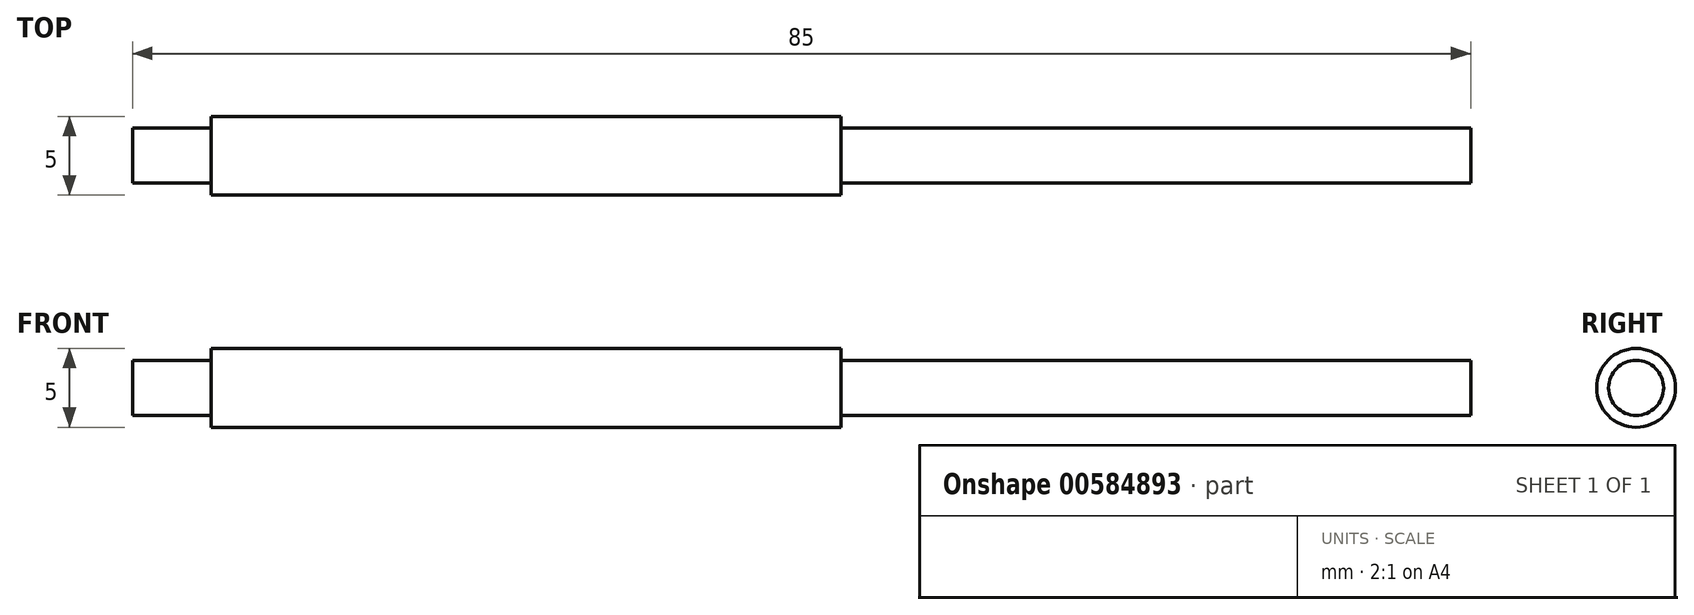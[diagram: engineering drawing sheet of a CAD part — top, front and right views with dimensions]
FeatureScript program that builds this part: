
annotation { "Feature Type Name" : "Feature", "Feature Type Description" : "" }
export const myFeature = defineFeature(function(context is Context, id is Id, definition is map)
    precondition{}
    {
        {
            var Q0;
            Q0=qCreatedBy(makeId("Top.planeOp"),FACE);
            var sketch = newSketch(context, id + "F0", { "sketchPlane" : qUnion([Q0])});
            skLineSegment(sketch, "E0.bottom", {"start": v(-20, 15) * mm, "end": v(20, 15) * mm});
            skLineSegment(sketch, "E0.top", {"start": v(-20, 0) * mm, "end": v(20, 0) * mm});
            skLineSegment(sketch, "E0.left", {"start": v(-20, 15) * mm, "end": v(-20, 0) * mm});
            skLineSegment(sketch, "E0.right", {"start": v(20, 15) * mm, "end": v(20, 0) * mm});
            skPoint(sketch, "E0.middle", {"position": v(0, 7.5) * mm});
            skSolve(sketch);
        }
        {
            var Q0;
            Q0 = qSketchRegion(id + "F0", true);
            var Q1;
            Q1=sQuery(id+"F0.wireOp",EDGE,"E0.top");
            revolve(context, id + "F1", {"entities" : qUnion([Q0]), "axis" : qUnion([Q1]), "revolveType" : RevolveType.FULL});
        }
        {
            var Q0;
            Q0=makeQuery(id+"F1.opRevolve","SWEPT_FACE",FACE,{"disambiguationData":[OSD([sQuery(id+"F0.wireOp",EDGE,"E0.right")])]});
            var sketch = newSketch(context, id + "F2", { "sketchPlane" : qUnion([Q0])});
            skCircle(sketch, "E1", {"center": v(0, 0) * mm, "radius": 1.75 * mm});
            skCircle(sketch, "E2.0", {"center": v(0, 0) * mm, "radius": 15 * mm});
            skLineSegment(sketch, "E3", {"start": v(-10.07, -11.12) * mm, "end": v(-0.6, -1.65) * mm});
            skLineSegment(sketch, "E4", {"start": v(-11.13, -10.06) * mm, "end": v(-1.65, -0.58) * mm});
            skLineSegment(sketch, "E5", {"start": v(-14.98, 0.75) * mm, "end": v(-1.58, 0.75) * mm});
            skLineSegment(sketch, "E6", {"start": v(-14.98, -0.75) * mm, "end": v(-1.58, -0.75) * mm});
            skLineSegment(sketch, "E7", {"start": v(-0.75, 14.98) * mm, "end": v(-0.75, 1.58) * mm});
            skLineSegment(sketch, "E8", {"start": v(0.75, -14.98) * mm, "end": v(0.75, -1.58) * mm});
            skLineSegment(sketch, "E9.MirrorCS", {"start": v(-0.75, -14.98) * mm, "end": v(-0.75, -1.58) * mm});
            skLineSegment(sketch, "E10.MirrorCS", {"start": v(11.13, -10.06) * mm, "end": v(1.65, -0.58) * mm});
            skLineSegment(sketch, "E11.MirrorCS", {"start": v(10.07, -11.12) * mm, "end": v(0.6, -1.65) * mm});
            skCircle(sketch, "E12", {"center": v(0, 0) * mm, "radius": 2.5 * mm});
            skLineSegment(sketch, "E13.trimOffspring", {"start": v(-1.65, 0.6) * mm, "end": v(-11.12, 10.07) * mm});
            skLineSegment(sketch, "E14.trimOffspring", {"start": v(0.58, 1.65) * mm, "end": v(10.06, 11.13) * mm});
            skLineSegment(sketch, "E15.trimOffspring", {"start": v(1.58, 0.75) * mm, "end": v(14.98, 0.75) * mm});
            skLineSegment(sketch, "E16.trimOffspring", {"start": v(-0.75, 1.58) * mm, "end": v(-0.75, 14.98) * mm});
            skLineSegment(sketch, "E17.trimOffspring", {"start": v(-0.75, -1.58) * mm, "end": v(-0.75, -14.98) * mm});
            skLineSegment(sketch, "E18.trimOffspring", {"start": v(-0.58, 1.65) * mm, "end": v(-10.06, 11.13) * mm});
            skLineSegment(sketch, "E19.trimOffspring", {"start": v(0.75, 1.58) * mm, "end": v(0.75, 14.98) * mm});
            skLineSegment(sketch, "E20.trimOffspring", {"start": v(1.65, 0.6) * mm, "end": v(11.12, 10.07) * mm});
            skLineSegment(sketch, "E21.trimOffspring", {"start": v(1.58, -0.75) * mm, "end": v(14.98, -0.75) * mm});
            skSolve(sketch);
        }
        {
            var Q0;
            {var subQ0=sQuery(id+"F2.wireOp",EDGE,"E1");var subQ8=makeQuery(id+"F2.imprint","INTERSECT",VERTEX,{"derivedFrom":[subQ0,sQuery(id+"F2.wireOp",EDGE,"E15.trimOffspring")]});Q0=makeQuery(id+"F2.imprint","IMPRINT",FACE,{"disambiguationData":[TD([[makeQuery(id+"F2.imprint","IMPRINT",EDGE,{"disambiguationData":[TD([[subQ8,1.0]])],"derivedFrom":subQ0}),1.0]])]});}
            var Q1;
            {var subQ0=sQuery(id+"F2.wireOp",EDGE,"E15.trimOffspring");var subQ1=sQuery(id+"F2.wireOp",EDGE,"E2.0");var subQ2=makeQuery(id+"F2.imprint","INTERSECT",VERTEX,{"derivedFrom":[subQ1,subQ0]});Q1=makeQuery(id+"F2.imprint","IMPRINT",FACE,{"disambiguationData":[TD([[makeQuery(id+"F2.imprint","IMPRINT",EDGE,{"disambiguationData":[TD([[subQ2,1.0]])],"derivedFrom":subQ1}),-1.0]])]});}
            var Q2;
            {var subQ0=sQuery(id+"F2.wireOp",EDGE,"E10.MirrorCS");var subQ1=sQuery(id+"F2.wireOp",EDGE,"E2.0");var subQ2=makeQuery(id+"F2.imprint","INTERSECT",VERTEX,{"derivedFrom":[subQ1,subQ0]});Q2=makeQuery(id+"F2.imprint","IMPRINT",FACE,{"disambiguationData":[TD([[makeQuery(id+"F2.imprint","IMPRINT",EDGE,{"disambiguationData":[TD([[subQ2,1.0]])],"derivedFrom":subQ1}),-1.0]])]});}
            var Q3;
            {var subQ0=sQuery(id+"F2.wireOp",EDGE,"E8");var subQ1=sQuery(id+"F2.wireOp",EDGE,"E2.0");var subQ2=makeQuery(id+"F2.imprint","INTERSECT",VERTEX,{"derivedFrom":[subQ1,subQ0]});Q3=makeQuery(id+"F2.imprint","IMPRINT",FACE,{"disambiguationData":[TD([[makeQuery(id+"F2.imprint","IMPRINT",EDGE,{"disambiguationData":[TD([[subQ2,1.0]])],"derivedFrom":subQ1}),-1.0]])]});}
            var Q4;
            {var subQ0=sQuery(id+"F2.wireOp",EDGE,"E3");var subQ1=sQuery(id+"F2.wireOp",EDGE,"E2.0");var subQ2=makeQuery(id+"F2.imprint","INTERSECT",VERTEX,{"derivedFrom":[subQ1,subQ0]});Q4=makeQuery(id+"F2.imprint","IMPRINT",FACE,{"disambiguationData":[TD([[makeQuery(id+"F2.imprint","IMPRINT",EDGE,{"disambiguationData":[TD([[subQ2,1.0]])],"derivedFrom":subQ1}),-1.0]])]});}
            var Q5;
            {var subQ0=sQuery(id+"F2.wireOp",EDGE,"E4");var subQ1=sQuery(id+"F2.wireOp",EDGE,"E2.0");var subQ2=makeQuery(id+"F2.imprint","INTERSECT",VERTEX,{"derivedFrom":[subQ1,subQ0]});Q5=makeQuery(id+"F2.imprint","IMPRINT",FACE,{"disambiguationData":[TD([[makeQuery(id+"F2.imprint","IMPRINT",EDGE,{"disambiguationData":[TD([[subQ2,-1.0]])],"derivedFrom":subQ1}),-1.0]])]});}
            var Q6;
            {var subQ0=sQuery(id+"F2.wireOp",EDGE,"E5");var subQ1=sQuery(id+"F2.wireOp",EDGE,"E2.0");var subQ2=makeQuery(id+"F2.imprint","INTERSECT",VERTEX,{"derivedFrom":[subQ1,subQ0]});Q6=makeQuery(id+"F2.imprint","IMPRINT",FACE,{"disambiguationData":[TD([[makeQuery(id+"F2.imprint","IMPRINT",EDGE,{"disambiguationData":[TD([[subQ2,-1.0]])],"derivedFrom":subQ1}),-1.0]])]});}
            var Q7;
            {var subQ0=sQuery(id+"F2.wireOp",EDGE,"E16.trimOffspring");var subQ1=sQuery(id+"F2.wireOp",EDGE,"E2.0");var subQ2=makeQuery(id+"F2.imprint","INTERSECT",VERTEX,{"derivedFrom":[subQ1,subQ0]});Q7=makeQuery(id+"F2.imprint","IMPRINT",FACE,{"disambiguationData":[TD([[makeQuery(id+"F2.imprint","IMPRINT",EDGE,{"disambiguationData":[TD([[subQ2,1.0]])],"derivedFrom":subQ1}),-1.0]])]});}
            var Q8;
            {var subQ0=sQuery(id+"F2.wireOp",EDGE,"E14.trimOffspring");var subQ1=sQuery(id+"F2.wireOp",EDGE,"E2.0");var subQ2=makeQuery(id+"F2.imprint","INTERSECT",VERTEX,{"derivedFrom":[subQ1,subQ0]});Q8=makeQuery(id+"F2.imprint","IMPRINT",FACE,{"disambiguationData":[TD([[makeQuery(id+"F2.imprint","IMPRINT",EDGE,{"disambiguationData":[TD([[subQ2,1.0]])],"derivedFrom":subQ1}),-1.0]])]});}
            extrude(context, id + "F3", {"entities" : qUnion([Q0, Q1, Q2, Q3, Q4, Q5, Q6, Q7, Q8]), "operationType" : NewBodyOperationType.REMOVE, "endBound" : BoundingType.THROUGH_ALL, "oppositeDirection" : true, "depth" : 25 * mm, "offsetDistance" : 25 * mm});
        }
        {
            var Q0;
            Q0=makeQuery(id+"F1.opRevolve","SWEPT_FACE",FACE,{"disambiguationData":[OSD([sQuery(id+"F0.wireOp",EDGE,"E0.left")])]});
            var sketch = newSketch(context, id + "F4", { "sketchPlane" : qUnion([Q0])});
            skCircle(sketch, "E22", {"center": v(0, 0) * mm, "radius": 0.75 * mm});
            skSolve(sketch);
        }
        {
            var Q0;
            {var subQ2=sQuery(id+"F0.wireOp",EDGE,"E0.left");var subQ3=makeQuery(id+"F1.opRevolve","SWEPT_FACE",FACE,{"disambiguationData":[OSD([subQ2])]});Q0=makeQuery(id+"F4.imprint","IMPRINT",FACE,{"disambiguationData":[TD([[makeQuery(id+"F4.imprint","IMPRINT",EDGE,{"derivedFrom":makeQuery(id+"F3.boolean.opBoolean","INTERSECT",EDGE,{"derivedFrom":[subQ3,makeQuery(id+"F3.opExtrude","SWEPT_FACE",FACE,{"disambiguationData":[OSD([sQuery(id+"F2.wireOp",EDGE,"E1")])]})]})}),1.0]])]});}
            var sketch = newSketch(context, id + "F5", { "sketchPlane" : qUnion([Q0])});
            skCircle(sketch, "E23.0", {"center": v(0, 0) * mm, "radius": 1.75 * mm});
            skCircle(sketch, "E24.cCircle", {"center": v(0, 0) * mm, "radius": 1.75 * mm, "construction": true});
            skLineSegment(sketch, "E24.0", {"start": v(0.78, -1.57) * mm, "end": v(-1.75, 0.11) * mm});
            skLineSegment(sketch, "E24.1", {"start": v(-1.75, 0.11) * mm, "end": v(0.97, 1.46) * mm});
            skLineSegment(sketch, "E24.2", {"start": v(0.97, 1.46) * mm, "end": v(0.78, -1.57) * mm});
            skSolve(sketch);
        }
        {
            var Q0;
            Q0=makeQuery(id+"F4.imprint","IMPRINT",FACE,{"disambiguationData":[TD([[makeQuery(id+"F4.imprint","IMPRINT",EDGE,{"derivedFrom":sQuery(id+"F4.wireOp",EDGE,"E22")}),-1.0]])]});
            var Q1;
            Q1=makeQuery(id+"F4.imprint","IMPRINT",FACE,{"disambiguationData":[TD([[makeQuery(id+"F4.imprint","IMPRINT",EDGE,{"derivedFrom":sQuery(id+"F4.wireOp",EDGE,"E22")}),1.0]])]});
            var Q2;
            Q2=sQuery(id+"F5.wireOp",EDGE,"E23.0");
            extrude(context, id + "F6", {"entities" : qUnion([Q0, Q1]), "operationType" : NewBodyOperationType.ADD, "surfaceEntities" : qUnion([Q2]), "depth" : 5 * mm, "offsetDistance" : 25 * mm, "hasSecondDirection" : true, "secondDirectionOppositeDirection" : true, "secondDirectionDepth" : 80 * mm});
        }
    });
